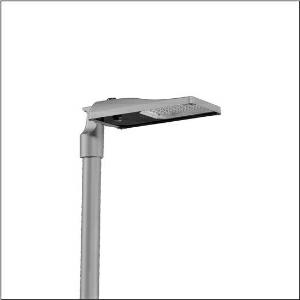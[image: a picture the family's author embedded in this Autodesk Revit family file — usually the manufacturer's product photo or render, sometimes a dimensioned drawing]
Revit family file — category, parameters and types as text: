
# Revit family: streetlight_sl_31_mini___st1_0a_5xh2d71t08ha_58cf
name_source: partatom
category: Lighting Fixtures
units: mm (PartAtom-declared; Revit-internal decimal feet)

## family parameters
Cut with Voids When Loaded = No
Host = Face
Light Source = No
Part Type = Normal
Room Calculation Point = No
Round Connector Dimension = Use Diameter
Shared = No

## types (1)
- --- (1 x LED, 7460 lm, 68.3 W, 2200K)
    Apparent Load = 68 VA
    CIE Flux Codes = 37 72 97 100 100
    Color Rendering = 70
    Color Temperature = 2200K
    Default Elevation = 1800 mm
    Description = Streetlight SL 31 mini D4i, Desk-Remote mast luminaire for post-top, side-entry; light control with lens of PMMA; light distribution: ST1.0a, direct asymmetric distribution, for standard-compliant lighting for roads and squares; LED: luminous flux: 7.460lm, light colour: 722, colour temperature: 2200K; luminous efficacy: 109,2lm/W; control: pre-setting: logarithmic dimming characteristic, flexible luminous flux parameterisation, time-dependent luminous flux control, constant luminous flux control, power reduction, intelligent temperature release in ECG and LED module, overheat protection; luminaire housing, of diecast aluminium, SITECO metallic grey (DB 702S), corrosivity category C5 high according to DIN EN ISO 12944; cover of toughened safety glass, transparent, mast flange of diecast aluminium, SITECO metallic grey (DB 702S), spigot size: 76/60mm, mast flange included unmounted; cable length: 8,5m, connection cable pre-assembled; mains connection: 220..240V, AC, 50/60Hz; power consumption (at start of service life): 68,3W / (at end of service life): 74,5W / (with reduced operation 50%): 29,2W; protection rating (complete): IP66; insulation class (complete): insulation class II (safety insulation); impact resistance: IK09; certification: CE, ENEC, ENEC+, VDE, UKCA, ZD4i; permissible operating ambient temperature for outdoor applications: -40..+50°C; packaging unit: 1 piece

Light Distribution: ST1.0a
    Height = 76 mm
    Lamp = 1 x LED
    Lamp Light Flux = 7460 lm
    Lamp Power = 68.3 W
    Lamp count = 1
    Length = 547 mm
    Luminous efficacy = 109 lm/W
    Manufacturer = Siteco
    ModVariant = No
    Model = 5XH2D71T08HA
    Number of Poles = 1
    OnlyDefault = Yes
    Power Factor = 1
    Product Name = Streetlight SL 31 mini | ST1.0a
    Product group = mast luminaire | pylon top
    ProductGroupID = 6100
    Protection Class = Protection class II
    Protection Degree = IP 66
    RLX_Detail_Level = 1
    RLX_Emergency_Light_Flux = 0 lm
    RLX_Emergency_Type = 0
    RLX_Emergency_Type_DB = No
    RlxData = <blob elided: 39357 chars, md5=a9da999c>
    Socket = socket
    Standby Power = 0 W
    System Light Flux = 7460 lm
    System Power = 68 W
    Type Comments = factory setting: luminous flux: 100 % | dim-lin: 254 | 692 mA
    Type Image = l_1300332.jpg
    URL = http://relux.com
    VarID = @adj_009359
    Voltage = 0 V
    Weight = 0.00 kg
    Width = 265 mm

## geometry (parser evidence)
native form markers: Blend x4, Sweep x11
no freeform markers — native parametric forms only
